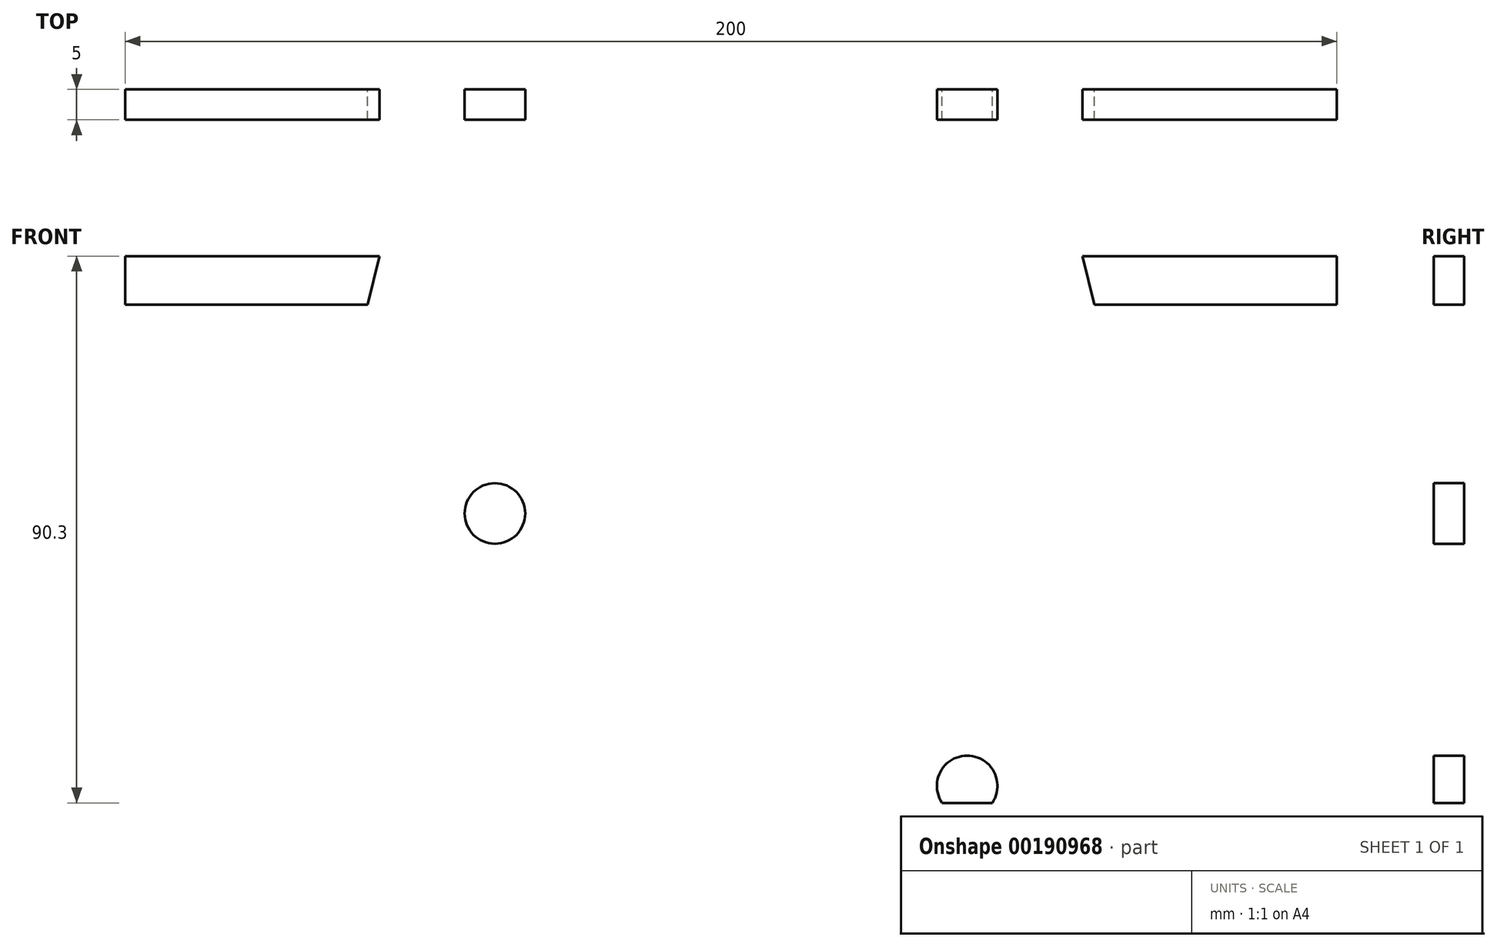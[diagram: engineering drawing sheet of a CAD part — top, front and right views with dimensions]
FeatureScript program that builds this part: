
annotation { "Feature Type Name" : "Feature", "Feature Type Description" : "" }
export const myFeature = defineFeature(function(context is Context, id is Id, definition is map)
    precondition{}
    {
        {
            var Q0;
            Q0=qCreatedBy(makeId("Front.planeOp"),FACE);
            var sketch = newSketch(context, id + "F0", { "sketchPlane" : qUnion([Q0])});
            skLineSegment(sketch, "E0.bottom", {"start": v(0, 0) * mm, "end": v(200, 0) * mm});
            skLineSegment(sketch, "E0.top", {"start": v(0, 130) * mm, "end": v(200, 130) * mm});
            skLineSegment(sketch, "E0.left", {"start": v(0, 0) * mm, "end": v(0, 130) * mm});
            skLineSegment(sketch, "E0.right", {"start": v(200, 0) * mm, "end": v(200, 130) * mm});
            skCircle(sketch, "E1", {"center": v(100, 65) * mm, "radius": 25.3 * mm});
            skCircle(sketch, "E2", {"center": v(61.03, 87.5) * mm, "radius": 5 * mm});
            skCircle(sketch, "E3", {"center": v(138.97, 42.5) * mm, "radius": 5 * mm});
            skLineSegment(sketch, "E4.bottom", {"start": v(100, 39.7) * mm, "end": v(200, 39.7) * mm});
            skLineSegment(sketch, "E4.top", {"start": v(100, 90.3) * mm, "end": v(200, 90.3) * mm});
            skLineSegment(sketch, "E4.left", {"start": v(100, 39.7) * mm, "end": v(100, 90.3) * mm});
            skLineSegment(sketch, "E4.right", {"start": v(200, 39.7) * mm, "end": v(200, 90.3) * mm});
            skLineSegment(sketch, "E5.bottom", {"start": v(200, 39.7) * mm, "end": v(159.7, 39.7) * mm});
            skLineSegment(sketch, "E5.top", {"start": v(200, 90.3) * mm, "end": v(159.7, 90.3) * mm});
            skLineSegment(sketch, "E5.right", {"start": v(159.7, 39.7) * mm, "end": v(159.7, 90.3) * mm});
            skCircle(sketch, "E6", {"center": v(180, 110) * mm, "radius": 5 * mm});
            skCircle(sketch, "E7", {"center": v(180, 20) * mm, "radius": 5 * mm});
            skCircle(sketch, "E8", {"center": v(20, 110) * mm, "radius": 5 * mm});
            skCircle(sketch, "E9", {"center": v(20, 20) * mm, "radius": 5 * mm});
            skCircle(sketch, "E10", {"center": v(180, 80) * mm, "radius": 5 * mm});
            skCircle(sketch, "E11", {"center": v(180, 50) * mm, "radius": 5 * mm});
            skLineSegment(sketch, "E12", {"start": v(61.03, 87.5) * mm, "end": v(100, 65) * mm});
            skLineSegment(sketch, "E13", {"start": v(100, 65) * mm, "end": v(138.97, 42.5) * mm});
            skLineSegment(sketch, "E14.bottom", {"start": v(0, -8) * mm, "end": v(40, -8) * mm});
            skLineSegment(sketch, "E14.top", {"start": v(0, 0) * mm, "end": v(40, 0) * mm});
            skLineSegment(sketch, "E14.left", {"start": v(0, -8) * mm, "end": v(0, 0) * mm});
            skLineSegment(sketch, "E14.right", {"start": v(40, -8) * mm, "end": v(40, 0) * mm});
            skLineSegment(sketch, "E15.bottom", {"start": v(200, -8) * mm, "end": v(160, -8) * mm});
            skLineSegment(sketch, "E15.top", {"start": v(200, 0) * mm, "end": v(160, 0) * mm});
            skLineSegment(sketch, "E15.left", {"start": v(200, -8) * mm, "end": v(200, 0) * mm});
            skLineSegment(sketch, "E15.right", {"start": v(160, -8) * mm, "end": v(160, 0) * mm});
            skLineSegment(sketch, "E16", {"start": v(40, -8) * mm, "end": v(42, 0) * mm});
            skLineSegment(sketch, "E17", {"start": v(160, -8) * mm, "end": v(158, 0) * mm});
            skLineSegment(sketch, "E18.bottom", {"start": v(0, 122) * mm, "end": v(40, 122) * mm});
            skLineSegment(sketch, "E18.top", {"start": v(0, 130) * mm, "end": v(40, 130) * mm});
            skLineSegment(sketch, "E18.left", {"start": v(0, 122) * mm, "end": v(0, 130) * mm});
            skLineSegment(sketch, "E18.right", {"start": v(40, 122) * mm, "end": v(40, 130) * mm});
            skLineSegment(sketch, "E19.bottom", {"start": v(200, 122) * mm, "end": v(160, 122) * mm});
            skLineSegment(sketch, "E19.top", {"start": v(200, 130) * mm, "end": v(160, 130) * mm});
            skLineSegment(sketch, "E19.left", {"start": v(200, 122) * mm, "end": v(200, 130) * mm});
            skLineSegment(sketch, "E19.right", {"start": v(160, 122) * mm, "end": v(160, 130) * mm});
            skLineSegment(sketch, "E20", {"start": v(40, 122) * mm, "end": v(42, 130) * mm});
            skLineSegment(sketch, "E21", {"start": v(160, 122) * mm, "end": v(158, 130) * mm});
            skLineSegment(sketch, "E22.bottom", {"start": v(29, 57.5) * mm, "end": v(34, 57.5) * mm});
            skLineSegment(sketch, "E22.top", {"start": v(29, 72.5) * mm, "end": v(34, 72.5) * mm});
            skLineSegment(sketch, "E22.left", {"start": v(29, 57.5) * mm, "end": v(29, 72.5) * mm});
            skLineSegment(sketch, "E22.right", {"start": v(34, 57.5) * mm, "end": v(34, 72.5) * mm});
            skLineSegment(sketch, "E23.bottom", {"start": v(29, 93.75) * mm, "end": v(34, 93.75) * mm});
            skLineSegment(sketch, "E23.top", {"start": v(29, 108.75) * mm, "end": v(34, 108.75) * mm});
            skLineSegment(sketch, "E23.left", {"start": v(29, 93.75) * mm, "end": v(29, 108.75) * mm});
            skLineSegment(sketch, "E23.right", {"start": v(34, 93.75) * mm, "end": v(34, 108.75) * mm});
            skLineSegment(sketch, "E24.bottom", {"start": v(29, 36.25) * mm, "end": v(34, 36.25) * mm});
            skLineSegment(sketch, "E24.top", {"start": v(29, 21.25) * mm, "end": v(34, 21.25) * mm});
            skLineSegment(sketch, "E24.left", {"start": v(29, 36.25) * mm, "end": v(29, 21.25) * mm});
            skLineSegment(sketch, "E24.right", {"start": v(34, 36.25) * mm, "end": v(34, 21.25) * mm});
            skSolve(sketch);
        }
        {
            var Q0;
            {var subQ22=sQuery(id+"F0.wireOp",EDGE,"E0.left");Q0=makeQuery(id+"F0.imprint","IMPRINT",FACE,{"disambiguationData":[TD([[makeQuery(id+"F0.imprint","IMPRINT",EDGE,{"derivedFrom":subQ22}),-1.0]])]});}
            var Q1;
            Q1=makeQuery(id+"F0.imprint","IMPRINT",FACE,{"disambiguationData":[TD([[makeQuery(id+"F0.imprint","IMPRINT",EDGE,{"derivedFrom":sQuery(id+"F0.wireOp",EDGE,"0B5afn8G-h0W6-BFAm-Bf3q-YGjXgToWp8EH.bottom")}),1.0]])]});
            var Q2;
            {var subQ0=sQuery(id+"F0.wireOp",EDGE,"JDXt8s4e-69hV-gc9z-V2TI-54T1ls7XA3z5.left");Q2=makeQuery(id+"F0.imprint","IMPRINT",FACE,{"disambiguationData":[TD([[makeQuery(id+"F0.imprint","IMPRINT",EDGE,{"derivedFrom":subQ0}),-1.0]])]});}
            var Q3;
            {var subQ0=sQuery(id+"F0.wireOp",EDGE,"JDXt8s4e-69hV-gc9z-V2TI-54T1ls7XA3z5.right");Q3=makeQuery(id+"F0.imprint","IMPRINT",FACE,{"disambiguationData":[TD([[makeQuery(id+"F0.imprint","IMPRINT",EDGE,{"derivedFrom":subQ0}),1.0]])]});}
            var Q4;
            Q4=makeQuery(id+"F0.imprint","IMPRINT",FACE,{"disambiguationData":[TD([[makeQuery(id+"F0.imprint","IMPRINT",EDGE,{"derivedFrom":sQuery(id+"F0.wireOp",EDGE,"E2")}),1.0]])]});
            var Q5;
            Q5=makeQuery(id+"F0.imprint","IMPRINT",FACE,{"disambiguationData":[TD([[makeQuery(id+"F0.imprint","IMPRINT",EDGE,{"derivedFrom":sQuery(id+"F0.wireOp",EDGE,"E18.bottom")}),1.0]])]});
            var Q6;
            Q6=makeQuery(id+"F0.imprint","IMPRINT",FACE,{"disambiguationData":[TD([[makeQuery(id+"F0.imprint","IMPRINT",EDGE,{"derivedFrom":sQuery(id+"F0.wireOp",EDGE,"E19.bottom")}),-1.0]])]});
            var Q7;
            {var subQ0=sQuery(id+"F0.wireOp",EDGE,"E19.right");Q7=makeQuery(id+"F0.imprint","IMPRINT",FACE,{"disambiguationData":[TD([[makeQuery(id+"F0.imprint","IMPRINT",EDGE,{"derivedFrom":subQ0}),1.0]])]});}
            var Q8;
            {var subQ0=sQuery(id+"F0.wireOp",EDGE,"E18.right");Q8=makeQuery(id+"F0.imprint","IMPRINT",FACE,{"disambiguationData":[TD([[makeQuery(id+"F0.imprint","IMPRINT",EDGE,{"derivedFrom":subQ0}),-1.0]])]});}
            var Q9;
            {var subQ0=sQuery(id+"F0.wireOp",EDGE,"E4.bottom");var subQ1=sQuery(id+"F0.wireOp",EDGE,"E3");var subQ2=makeQuery(id+"F0.imprint","INTERSECT",VERTEX,{"disambiguationData":[OD(0.0)],"derivedFrom":[subQ1,subQ0]});Q9=makeQuery(id+"F0.imprint","IMPRINT",FACE,{"disambiguationData":[TD([[makeQuery(id+"F0.imprint","IMPRINT",EDGE,{"disambiguationData":[TD([[subQ2,-1.0]])],"derivedFrom":subQ1}),1.0]])]});}
            extrude(context, id + "F1", {"entities" : qUnion([Q0, Q1, Q2, Q3, Q4, Q5, Q6, Q7, Q8, Q9]), "depth" : 5 * mm});
        }
    });
